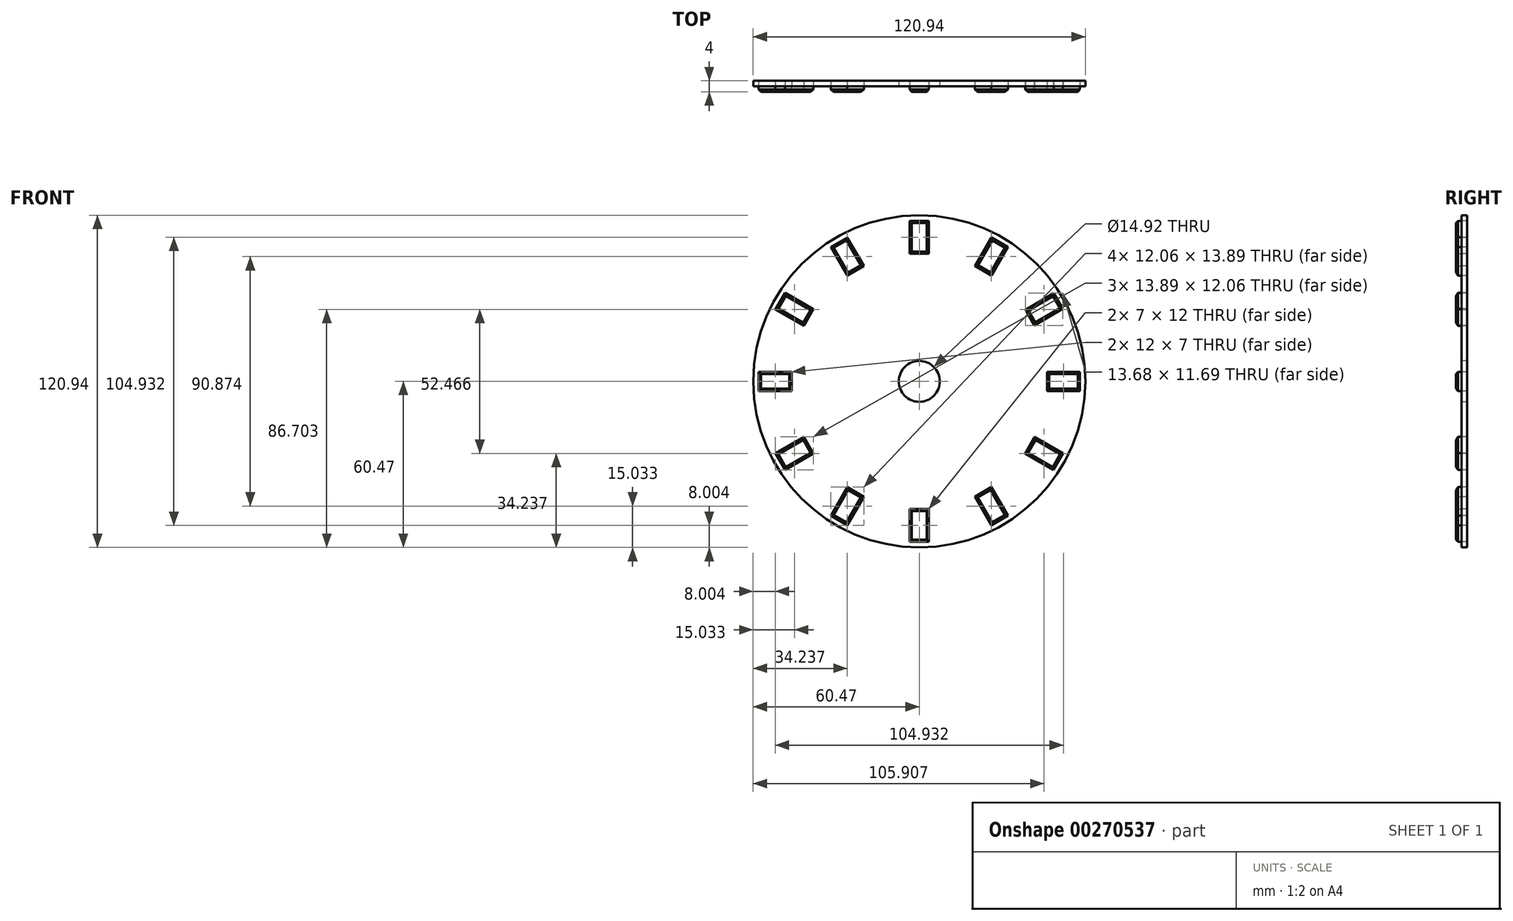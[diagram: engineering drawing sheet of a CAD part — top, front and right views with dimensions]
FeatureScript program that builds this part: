
annotation { "Feature Type Name" : "Feature", "Feature Type Description" : "" }
export const myFeature = defineFeature(function(context is Context, id is Id, definition is map)
    precondition{}
    {
        {
            var Q0;
            Q0=qCreatedBy(makeId("Front.planeOp"),FACE);
            var sketch = newSketch(context, id + "F0", { "sketchPlane" : qUnion([Q0])});
            skCircle(sketch, "E0", {"center": v(0, 0) * mm, "radius": 60.47 * mm});
            skLineSegment(sketch, "E1", {"start": v(0, 0) * mm, "end": v(23.27, 40.3) * mm});
            skLineSegment(sketch, "E2", {"start": v(0, 0) * mm, "end": v(-40.24, 23.23) * mm});
            skLineSegment(sketch, "E3", {"start": v(0, 0) * mm, "end": v(-40.24, -23.23) * mm});
            skLineSegment(sketch, "E4", {"start": v(-60.47, 0) * mm, "end": v(-58.47, 0) * mm});
            skLineSegment(sketch, "E5", {"start": v(0, 0) * mm, "end": v(40.24, -23.23) * mm});
            skLineSegment(sketch, "E6", {"start": v(0, 0) * mm, "end": v(0, 46.47) * mm});
            skLineSegment(sketch, "E7", {"start": v(0, 0) * mm, "end": v(46.47, 0) * mm});
            skLineSegment(sketch, "E8", {"start": v(0, 0) * mm, "end": v(0, -46.47) * mm});
            skLineSegment(sketch, "E9", {"start": v(0, 0) * mm, "end": v(40.24, 23.23) * mm});
            skLineSegment(sketch, "E10", {"start": v(0, 0) * mm, "end": v(23.23, -40.24) * mm});
            skLineSegment(sketch, "E11", {"start": v(0, 0) * mm, "end": v(-23.23, -40.24) * mm});
            skLineSegment(sketch, "E12", {"start": v(0, 0) * mm, "end": v(-23.23, 40.24) * mm});
            skLineSegment(sketch, "E13", {"start": v(52.28, 26.39) * mm, "end": v(41.88, 20.39) * mm});
            skLineSegment(sketch, "E14.MirrorCS", {"start": v(48.99, 32.08) * mm, "end": v(38.6, 26.08) * mm});
            skLineSegment(sketch, "E15", {"start": v(48.99, 32.08) * mm, "end": v(52.28, 26.39) * mm});
            skLineSegment(sketch, "E16", {"start": v(38.6, 26.08) * mm, "end": v(41.88, 20.39) * mm});
            skLineSegment(sketch, "E17", {"start": v(26.3, 38.55) * mm, "end": v(32.3, 48.94) * mm});
            skLineSegment(sketch, "E18.MirrorCS", {"start": v(20.24, 42.05) * mm, "end": v(26.24, 52.44) * mm});
            skLineSegment(sketch, "E19", {"start": v(20.24, 42.05) * mm, "end": v(26.3, 38.55) * mm});
            skLineSegment(sketch, "E20", {"start": v(26.24, 52.44) * mm, "end": v(32.3, 48.94) * mm});
            skLineSegment(sketch, "E21", {"start": v(3.5, 58.47) * mm, "end": v(3.5, 46.47) * mm});
            skLineSegment(sketch, "E22.MirrorCS", {"start": v(-3.5, 58.47) * mm, "end": v(-3.5, 46.47) * mm});
            skLineSegment(sketch, "E23", {"start": v(-3.5, 46.47) * mm, "end": v(3.5, 46.47) * mm});
            skLineSegment(sketch, "E24", {"start": v(3.5, 58.47) * mm, "end": v(-3.5, 58.47) * mm});
            skLineSegment(sketch, "E25", {"start": v(-52.38, 26.2) * mm, "end": v(-42, 20.2) * mm});
            skLineSegment(sketch, "E26", {"start": v(-52.38, -26.2) * mm, "end": v(-42, -20.2) * mm});
            skLineSegment(sketch, "E27", {"start": v(-26.2, -52.38) * mm, "end": v(-20.2, -42) * mm});
            skLineSegment(sketch, "E28", {"start": v(-3.5, -46.47) * mm, "end": v(-3.5, -58.47) * mm});
            skLineSegment(sketch, "E29", {"start": v(20.2, -42) * mm, "end": v(26.2, -52.38) * mm});
            skLineSegment(sketch, "E30", {"start": v(38.5, -26.26) * mm, "end": v(48.88, -32.26) * mm});
            skLineSegment(sketch, "E31", {"start": v(46.47, -3.5) * mm, "end": v(58.47, -3.5) * mm});
            skLineSegment(sketch, "E32", {"start": v(-26.2, 52.38) * mm, "end": v(-20.2, 42) * mm});
            skLineSegment(sketch, "E33.MirrorCS", {"start": v(-32.26, 48.88) * mm, "end": v(-26.26, 38.5) * mm});
            skLineSegment(sketch, "E34.MirrorCS", {"start": v(-48.88, 32.26) * mm, "end": v(-38.5, 26.26) * mm});
            skLineSegment(sketch, "E35.MirrorCS", {"start": v(-30.23, 52.37) * mm, "end": v(-29.23, 50.63) * mm});
            skLineSegment(sketch, "E36.MirrorCS", {"start": v(-48.88, -32.26) * mm, "end": v(-38.5, -26.26) * mm});
            skLineSegment(sketch, "E37.MirrorCS", {"start": v(0, 0) * mm, "end": v(-60.47, 0) * mm});
            skLineSegment(sketch, "E38.MirrorCS", {"start": v(0, 0) * mm, "end": v(-46.47, 0) * mm});
            skLineSegment(sketch, "E39.MirrorCS", {"start": v(-32.26, -48.88) * mm, "end": v(-26.26, -38.5) * mm});
            skLineSegment(sketch, "E40.MirrorCS", {"start": v(3.5, -46.47) * mm, "end": v(3.5, -58.47) * mm});
            skLineSegment(sketch, "E41.MirrorCS", {"start": v(26.26, -38.5) * mm, "end": v(32.26, -48.88) * mm});
            skLineSegment(sketch, "E42.MirrorCS", {"start": v(42, -20.2) * mm, "end": v(52.38, -26.2) * mm});
            skLineSegment(sketch, "E43.MirrorCS", {"start": v(46.47, 3.5) * mm, "end": v(58.47, 3.5) * mm});
            skLineSegment(sketch, "E44.MirrorCS", {"start": v(-41.55, 3.5) * mm, "end": v(-41.52, 3.5) * mm});
            skLineSegment(sketch, "E45", {"start": v(-38.5, 26.26) * mm, "end": v(-42, 20.2) * mm});
            skLineSegment(sketch, "E46", {"start": v(-48.88, 32.26) * mm, "end": v(-52.38, 26.2) * mm});
            skLineSegment(sketch, "E47", {"start": v(-42, -20.2) * mm, "end": v(-38.5, -26.26) * mm});
            skLineSegment(sketch, "E48", {"start": v(-52.38, -26.2) * mm, "end": v(-48.88, -32.26) * mm});
            skLineSegment(sketch, "E49", {"start": v(-26.26, -38.5) * mm, "end": v(-20.2, -42) * mm});
            skLineSegment(sketch, "E50", {"start": v(-26.2, -52.38) * mm, "end": v(-32.26, -48.88) * mm});
            skLineSegment(sketch, "E51", {"start": v(-3.5, -58.47) * mm, "end": v(3.5, -58.47) * mm});
            skLineSegment(sketch, "E52", {"start": v(3.5, -46.47) * mm, "end": v(-3.5, -46.47) * mm});
            skLineSegment(sketch, "E53", {"start": v(20.2, -42) * mm, "end": v(26.26, -38.5) * mm});
            skLineSegment(sketch, "E54", {"start": v(32.26, -48.88) * mm, "end": v(26.2, -52.38) * mm});
            skLineSegment(sketch, "E55", {"start": v(38.5, -26.26) * mm, "end": v(42, -20.2) * mm});
            skLineSegment(sketch, "E56", {"start": v(52.38, -26.2) * mm, "end": v(48.88, -32.26) * mm});
            skLineSegment(sketch, "E57", {"start": v(58.47, -3.5) * mm, "end": v(58.47, 3.5) * mm});
            skLineSegment(sketch, "E58", {"start": v(46.47, 3.5) * mm, "end": v(46.47, -3.5) * mm});
            skLineSegment(sketch, "E59", {"start": v(-32.26, 48.88) * mm, "end": v(-26.2, 52.38) * mm});
            skLineSegment(sketch, "E60", {"start": v(-20.2, 42) * mm, "end": v(-26.26, 38.5) * mm});
            skLineSegment(sketch, "E61", {"start": v(-58.47, 3.5) * mm, "end": v(-46.47, 3.5) * mm});
            skLineSegment(sketch, "E62.MirrorCS", {"start": v(-58.47, -3.5) * mm, "end": v(-46.47, -3.5) * mm});
            skLineSegment(sketch, "E63", {"start": v(-58.47, 3.5) * mm, "end": v(-58.47, -3.5) * mm});
            skLineSegment(sketch, "E64", {"start": v(-46.47, 3.5) * mm, "end": v(-46.47, -3.5) * mm});
            skLineSegment(sketch, "E65.trimOffspring", {"start": v(-50.63, 29.23) * mm, "end": v(-52.37, 30.23) * mm});
            skLineSegment(sketch, "E66.trimOffspring", {"start": v(-29.23, 50.63) * mm, "end": v(-30.23, 52.37) * mm});
            skLineSegment(sketch, "E67.trimOffspring", {"start": v(0, 58.47) * mm, "end": v(0, 60.47) * mm});
            skLineSegment(sketch, "E68.trimOffspring", {"start": v(29.27, 50.7) * mm, "end": v(30.27, 52.42) * mm});
            skLineSegment(sketch, "E69.trimOffspring", {"start": v(50.63, 29.23) * mm, "end": v(52.37, 30.23) * mm});
            skLineSegment(sketch, "E70.trimOffspring", {"start": v(58.47, 0) * mm, "end": v(60.47, 0) * mm});
            skLineSegment(sketch, "E71.trimOffspring", {"start": v(50.63, -29.23) * mm, "end": v(52.37, -30.23) * mm});
            skLineSegment(sketch, "E72.trimOffspring", {"start": v(29.23, -50.63) * mm, "end": v(30.23, -52.37) * mm});
            skLineSegment(sketch, "E73.trimOffspring", {"start": v(0, -58.47) * mm, "end": v(0, -60.47) * mm});
            skLineSegment(sketch, "E74.trimOffspring", {"start": v(-29.23, -50.63) * mm, "end": v(-30.23, -52.37) * mm});
            skLineSegment(sketch, "E75.trimOffspring", {"start": v(-50.63, -29.23) * mm, "end": v(-52.37, -30.23) * mm});
            skLineSegment(sketch, "E76.trimOffspring", {"start": v(-46.47, 0) * mm, "end": v(0, 0) * mm});
            skLineSegment(sketch, "E77.trimOffspring", {"start": v(-23.23, 40.24) * mm, "end": v(0, 0) * mm});
            skLineSegment(sketch, "E78.trimOffspring", {"start": v(-58.47, 0) * mm, "end": v(-60.47, 0) * mm});
            skSolve(sketch);
        }
        {
            var Q0;
            {var subQ2=sQuery(id+"F0.wireOp",EDGE,"E25");Q0=makeQuery(id+"F0.imprint","IMPRINT",FACE,{"disambiguationData":[TD([[makeQuery(id+"F0.imprint","IMPRINT",EDGE,{"derivedFrom":subQ2}),1.0]])]});}
            var Q1;
            {var subQ1=sQuery(id+"F0.wireOp",EDGE,"E32");Q1=makeQuery(id+"F0.imprint","IMPRINT",FACE,{"disambiguationData":[TD([[makeQuery(id+"F0.imprint","IMPRINT",EDGE,{"derivedFrom":subQ1}),-1.0]])]});}
            var Q2;
            {var subQ2=sQuery(id+"F0.wireOp",EDGE,"E21");Q2=makeQuery(id+"F0.imprint","IMPRINT",FACE,{"disambiguationData":[TD([[makeQuery(id+"F0.imprint","IMPRINT",EDGE,{"derivedFrom":subQ2}),-1.0]])]});}
            var Q3;
            {var subQ2=sQuery(id+"F0.wireOp",EDGE,"E17");Q3=makeQuery(id+"F0.imprint","IMPRINT",FACE,{"disambiguationData":[TD([[makeQuery(id+"F0.imprint","IMPRINT",EDGE,{"derivedFrom":subQ2}),1.0]])]});}
            var Q4;
            {var subQ1=sQuery(id+"F0.wireOp",EDGE,"E13");Q4=makeQuery(id+"F0.imprint","IMPRINT",FACE,{"disambiguationData":[TD([[makeQuery(id+"F0.imprint","IMPRINT",EDGE,{"derivedFrom":subQ1}),-1.0]])]});}
            var Q5;
            {var subQ5=sQuery(id+"F0.wireOp",EDGE,"E31");Q5=makeQuery(id+"F0.imprint","IMPRINT",FACE,{"disambiguationData":[TD([[makeQuery(id+"F0.imprint","IMPRINT",EDGE,{"derivedFrom":subQ5}),1.0]])]});}
            var Q6;
            {var subQ3=sQuery(id+"F0.wireOp",EDGE,"E30");Q6=makeQuery(id+"F0.imprint","IMPRINT",FACE,{"disambiguationData":[TD([[makeQuery(id+"F0.imprint","IMPRINT",EDGE,{"derivedFrom":subQ3}),1.0]])]});}
            var Q7;
            {var subQ3=sQuery(id+"F0.wireOp",EDGE,"E29");Q7=makeQuery(id+"F0.imprint","IMPRINT",FACE,{"disambiguationData":[TD([[makeQuery(id+"F0.imprint","IMPRINT",EDGE,{"derivedFrom":subQ3}),1.0]])]});}
            var Q8;
            {var subQ3=sQuery(id+"F0.wireOp",EDGE,"E28");Q8=makeQuery(id+"F0.imprint","IMPRINT",FACE,{"disambiguationData":[TD([[makeQuery(id+"F0.imprint","IMPRINT",EDGE,{"derivedFrom":subQ3}),1.0]])]});}
            var Q9;
            {var subQ2=sQuery(id+"F0.wireOp",EDGE,"E27");Q9=makeQuery(id+"F0.imprint","IMPRINT",FACE,{"disambiguationData":[TD([[makeQuery(id+"F0.imprint","IMPRINT",EDGE,{"derivedFrom":subQ2}),1.0]])]});}
            var Q10;
            {var subQ3=sQuery(id+"F0.wireOp",EDGE,"E26");Q10=makeQuery(id+"F0.imprint","IMPRINT",FACE,{"disambiguationData":[TD([[makeQuery(id+"F0.imprint","IMPRINT",EDGE,{"derivedFrom":subQ3}),-1.0]])]});}
            var Q11;
            {var subQ0=sQuery(id+"F0.wireOp",EDGE,"E37.MirrorCS");Q11=makeQuery(id+"F0.imprint","IMPRINT",FACE,{"disambiguationData":[TD([[makeQuery(id+"F0.imprint","IMPRINT",EDGE,{"derivedFrom":subQ0}),-1.0]])]});}
            var Q12;
            {var subQ0=sQuery(id+"F0.wireOp",EDGE,"E37.MirrorCS");Q12=makeQuery(id+"F0.imprint","IMPRINT",FACE,{"disambiguationData":[TD([[makeQuery(id+"F0.imprint","IMPRINT",EDGE,{"derivedFrom":subQ0}),1.0]])]});}
            extrude(context, id + "F1", {"entities" : qUnion([Q0, Q1, Q2, Q3, Q4, Q5, Q6, Q7, Q8, Q9, Q10, Q11, Q12]), "depth" : 2 * mm});
        }
        {
            var Q0;
            Q0 = qSketchRegion(id + "F0", true);
            extrude(context, id + "F2", {"entities" : qUnion([Q0]), "oppositeDirection" : true, "depth" : 2 * mm});
        }
        {
            var Q0;
            Q0=qCreatedBy(makeId("Front.planeOp"),FACE);
            var sketch = newSketch(context, id + "F3", { "sketchPlane" : qUnion([Q0])});
            skCircle(sketch, "E79", {"center": v(0, 0) * mm, "radius": 7.46 * mm});
            skCircle(sketch, "E80", {"center": v(46.57, 14.57) * mm, "radius": 2.5 * mm});
            skCircle(sketch, "E81", {"center": v(-47.92, -12.77) * mm, "radius": 2.5 * mm});
            skSolve(sketch);
        }
        {
            var Q0;
            Q0=makeQuery(id+"F3.imprint","IMPRINT",FACE,{"disambiguationData":[TD([[makeQuery(id+"F3.imprint","IMPRINT",EDGE,{"derivedFrom":sQuery(id+"F3.wireOp",EDGE,"E79")}),1.0]])]});
            extrude(context, id + "F4", {"entities" : qUnion([Q0]), "operationType" : NewBodyOperationType.REMOVE, "oppositeDirection" : true, "depth" : 5 * mm});
        }
        {
            var Q0;
            Q0=sQuery(id+"F3.wireOp",EDGE,"E80");
            var Q1;
            Q1=sQuery(id+"F3.wireOp",EDGE,"E81");
            extrude(context, id + "F5", {"bodyType" : ToolBodyType.SURFACE, "surfaceEntities" : qUnion([Q0, Q1]), "oppositeDirection" : true, "depth" : 25 * mm});
        }
        {
            var Q0;
            Q0=makeQuery(id+"F1.opExtrude","CAP_FACE",FACE,{"disambiguationData":[OSD([sQuery(id+"F0.wireOp",EDGE,"E31"),sQuery(id+"F0.wireOp",EDGE,"E43.MirrorCS"),sQuery(id+"F0.wireOp",EDGE,"E57"),sQuery(id+"F0.wireOp",EDGE,"E58")])],"isStart":true});
            var Q1;
            Q1=makeQuery(id+"F1.opExtrude","CAP_FACE",FACE,{"disambiguationData":[OSD([sQuery(id+"F0.wireOp",EDGE,"E13"),sQuery(id+"F0.wireOp",EDGE,"E14.MirrorCS"),sQuery(id+"F0.wireOp",EDGE,"E15"),sQuery(id+"F0.wireOp",EDGE,"E16")])],"isStart":true});
            var Q2;
            Q2=makeQuery(id+"F1.opExtrude","CAP_FACE",FACE,{"disambiguationData":[OSD([sQuery(id+"F0.wireOp",EDGE,"E17"),sQuery(id+"F0.wireOp",EDGE,"E18.MirrorCS"),sQuery(id+"F0.wireOp",EDGE,"E19"),sQuery(id+"F0.wireOp",EDGE,"E20")])],"isStart":true});
            var Q3;
            Q3=makeQuery(id+"F1.opExtrude","CAP_FACE",FACE,{"disambiguationData":[OSD([sQuery(id+"F0.wireOp",EDGE,"E21"),sQuery(id+"F0.wireOp",EDGE,"E22.MirrorCS"),sQuery(id+"F0.wireOp",EDGE,"E23"),sQuery(id+"F0.wireOp",EDGE,"E24")])],"isStart":true});
            var Q4;
            Q4=makeQuery(id+"F1.opExtrude","CAP_FACE",FACE,{"disambiguationData":[OSD([sQuery(id+"F0.wireOp",EDGE,"E32"),sQuery(id+"F0.wireOp",EDGE,"E33.MirrorCS"),sQuery(id+"F0.wireOp",EDGE,"E59"),sQuery(id+"F0.wireOp",EDGE,"E60")])],"isStart":true});
            var Q5;
            Q5=makeQuery(id+"F1.opExtrude","CAP_FACE",FACE,{"disambiguationData":[OSD([sQuery(id+"F0.wireOp",EDGE,"E25"),sQuery(id+"F0.wireOp",EDGE,"E34.MirrorCS"),sQuery(id+"F0.wireOp",EDGE,"E45"),sQuery(id+"F0.wireOp",EDGE,"E46")])],"isStart":true});
            var Q6;
            Q6=makeQuery(id+"F1.opExtrude","CAP_FACE",FACE,{"disambiguationData":[OSD([sQuery(id+"F0.wireOp",EDGE,"E61"),sQuery(id+"F0.wireOp",EDGE,"E62.MirrorCS"),sQuery(id+"F0.wireOp",EDGE,"E63"),sQuery(id+"F0.wireOp",EDGE,"E64")])],"isStart":true});
            var Q7;
            Q7=makeQuery(id+"F1.opExtrude","CAP_FACE",FACE,{"disambiguationData":[OSD([sQuery(id+"F0.wireOp",EDGE,"E26"),sQuery(id+"F0.wireOp",EDGE,"E36.MirrorCS"),sQuery(id+"F0.wireOp",EDGE,"E47"),sQuery(id+"F0.wireOp",EDGE,"E48")])],"isStart":true});
            var Q8;
            Q8=makeQuery(id+"F1.opExtrude","CAP_FACE",FACE,{"disambiguationData":[OSD([sQuery(id+"F0.wireOp",EDGE,"E27"),sQuery(id+"F0.wireOp",EDGE,"E39.MirrorCS"),sQuery(id+"F0.wireOp",EDGE,"E49"),sQuery(id+"F0.wireOp",EDGE,"E50")])],"isStart":true});
            var Q9;
            Q9=makeQuery(id+"F1.opExtrude","CAP_FACE",FACE,{"disambiguationData":[OSD([sQuery(id+"F0.wireOp",EDGE,"E28"),sQuery(id+"F0.wireOp",EDGE,"E40.MirrorCS"),sQuery(id+"F0.wireOp",EDGE,"E51"),sQuery(id+"F0.wireOp",EDGE,"E52")])],"isStart":true});
            var Q10;
            Q10=makeQuery(id+"F1.opExtrude","CAP_FACE",FACE,{"disambiguationData":[OSD([sQuery(id+"F0.wireOp",EDGE,"E29"),sQuery(id+"F0.wireOp",EDGE,"E41.MirrorCS"),sQuery(id+"F0.wireOp",EDGE,"E53"),sQuery(id+"F0.wireOp",EDGE,"E54")])],"isStart":true});
            var Q11;
            Q11=makeQuery(id+"F1.opExtrude","CAP_FACE",FACE,{"disambiguationData":[OSD([sQuery(id+"F0.wireOp",EDGE,"E30"),sQuery(id+"F0.wireOp",EDGE,"E42.MirrorCS"),sQuery(id+"F0.wireOp",EDGE,"E55"),sQuery(id+"F0.wireOp",EDGE,"E56")])],"isStart":true});
            extrude(context, id + "F6", {"entities" : qUnion([Q0, Q1, Q2, Q3, Q4, Q5, Q6, Q7, Q8, Q9, Q10, Q11]), "depth" : 2 * mm});
        }
        {
            var Q0;
            Q0=makeQuery(id+"F1.opExtrude","CAP_EDGE",EDGE,{"disambiguationData":[OSD([sQuery(id+"F0.wireOp",EDGE,"E25")])],"isStart":false});
            var Q1;
            Q1=makeQuery(id+"F1.opExtrude","CAP_EDGE",EDGE,{"disambiguationData":[OSD([sQuery(id+"F0.wireOp",EDGE,"E34.MirrorCS")])],"isStart":false});
            var Q2;
            Q2=makeQuery(id+"F1.opExtrude","CAP_EDGE",EDGE,{"disambiguationData":[OSD([sQuery(id+"F0.wireOp",EDGE,"E33.MirrorCS")])],"isStart":false});
            var Q3;
            Q3=makeQuery(id+"F1.opExtrude","CAP_EDGE",EDGE,{"disambiguationData":[OSD([sQuery(id+"F0.wireOp",EDGE,"E32")])],"isStart":false});
            var Q4;
            Q4=makeQuery(id+"F1.opExtrude","CAP_EDGE",EDGE,{"disambiguationData":[OSD([sQuery(id+"F0.wireOp",EDGE,"E22.MirrorCS")])],"isStart":false});
            var Q5;
            Q5=makeQuery(id+"F1.opExtrude","CAP_EDGE",EDGE,{"disambiguationData":[OSD([sQuery(id+"F0.wireOp",EDGE,"E21")])],"isStart":false});
            var Q6;
            Q6=makeQuery(id+"F1.opExtrude","CAP_EDGE",EDGE,{"disambiguationData":[OSD([sQuery(id+"F0.wireOp",EDGE,"E18.MirrorCS")])],"isStart":false});
            var Q7;
            Q7=makeQuery(id+"F1.opExtrude","CAP_EDGE",EDGE,{"disambiguationData":[OSD([sQuery(id+"F0.wireOp",EDGE,"E17")])],"isStart":false});
            var Q8;
            Q8=makeQuery(id+"F1.opExtrude","CAP_EDGE",EDGE,{"disambiguationData":[OSD([sQuery(id+"F0.wireOp",EDGE,"E13")])],"isStart":false});
            var Q9;
            Q9=makeQuery(id+"F1.opExtrude","CAP_EDGE",EDGE,{"disambiguationData":[OSD([sQuery(id+"F0.wireOp",EDGE,"E14.MirrorCS")])],"isStart":false});
            var Q10;
            Q10=makeQuery(id+"F1.opExtrude","CAP_EDGE",EDGE,{"disambiguationData":[OSD([sQuery(id+"F0.wireOp",EDGE,"E31")])],"isStart":false});
            var Q11;
            Q11=makeQuery(id+"F1.opExtrude","CAP_EDGE",EDGE,{"disambiguationData":[OSD([sQuery(id+"F0.wireOp",EDGE,"E30")])],"isStart":false});
            var Q12;
            Q12=makeQuery(id+"F1.opExtrude","CAP_EDGE",EDGE,{"disambiguationData":[OSD([sQuery(id+"F0.wireOp",EDGE,"E29")])],"isStart":false});
            var Q13;
            Q13=makeQuery(id+"F1.opExtrude","CAP_EDGE",EDGE,{"disambiguationData":[OSD([sQuery(id+"F0.wireOp",EDGE,"E40.MirrorCS")])],"isStart":false});
            var Q14;
            Q14=makeQuery(id+"F1.opExtrude","CAP_EDGE",EDGE,{"disambiguationData":[OSD([sQuery(id+"F0.wireOp",EDGE,"E51")])],"isStart":false});
            var Q15;
            Q15=makeQuery(id+"F1.opExtrude","CAP_EDGE",EDGE,{"disambiguationData":[OSD([sQuery(id+"F0.wireOp",EDGE,"E28")])],"isStart":false});
            var Q16;
            Q16=makeQuery(id+"F1.opExtrude","CAP_EDGE",EDGE,{"disambiguationData":[OSD([sQuery(id+"F0.wireOp",EDGE,"E52")])],"isStart":false});
            var Q17;
            Q17=makeQuery(id+"F1.opExtrude","CAP_EDGE",EDGE,{"disambiguationData":[OSD([sQuery(id+"F0.wireOp",EDGE,"E49")])],"isStart":false});
            var Q18;
            Q18=makeQuery(id+"F1.opExtrude","CAP_EDGE",EDGE,{"disambiguationData":[OSD([sQuery(id+"F0.wireOp",EDGE,"E27")])],"isStart":false});
            var Q19;
            Q19=makeQuery(id+"F1.opExtrude","CAP_EDGE",EDGE,{"disambiguationData":[OSD([sQuery(id+"F0.wireOp",EDGE,"E50")])],"isStart":false});
            var Q20;
            Q20=makeQuery(id+"F1.opExtrude","CAP_EDGE",EDGE,{"disambiguationData":[OSD([sQuery(id+"F0.wireOp",EDGE,"E39.MirrorCS")])],"isStart":false});
            var Q21;
            Q21=makeQuery(id+"F1.opExtrude","CAP_EDGE",EDGE,{"disambiguationData":[OSD([sQuery(id+"F0.wireOp",EDGE,"E36.MirrorCS")])],"isStart":false});
            var Q22;
            Q22=makeQuery(id+"F1.opExtrude","CAP_EDGE",EDGE,{"disambiguationData":[OSD([sQuery(id+"F0.wireOp",EDGE,"E48")])],"isStart":false});
            var Q23;
            Q23=makeQuery(id+"F1.opExtrude","CAP_EDGE",EDGE,{"disambiguationData":[OSD([sQuery(id+"F0.wireOp",EDGE,"E26")])],"isStart":false});
            var Q24;
            Q24=makeQuery(id+"F1.opExtrude","CAP_EDGE",EDGE,{"disambiguationData":[OSD([sQuery(id+"F0.wireOp",EDGE,"E47")])],"isStart":false});
            var Q25;
            Q25=makeQuery(id+"F1.opExtrude","CAP_FACE",FACE,{"disambiguationData":[OSD([sQuery(id+"F0.wireOp",EDGE,"E61"),sQuery(id+"F0.wireOp",EDGE,"E62.MirrorCS"),sQuery(id+"F0.wireOp",EDGE,"E63"),sQuery(id+"F0.wireOp",EDGE,"E64")])],"isStart":false});
            var Q26;
            Q26=makeQuery(id+"F1.opExtrude","CAP_FACE",FACE,{"disambiguationData":[OSD([sQuery(id+"F0.wireOp",EDGE,"E25"),sQuery(id+"F0.wireOp",EDGE,"E34.MirrorCS"),sQuery(id+"F0.wireOp",EDGE,"E45"),sQuery(id+"F0.wireOp",EDGE,"E46")])],"isStart":false});
            var Q27;
            Q27=makeQuery(id+"F1.opExtrude","CAP_FACE",FACE,{"disambiguationData":[OSD([sQuery(id+"F0.wireOp",EDGE,"E32"),sQuery(id+"F0.wireOp",EDGE,"E33.MirrorCS"),sQuery(id+"F0.wireOp",EDGE,"E59"),sQuery(id+"F0.wireOp",EDGE,"E60")])],"isStart":false});
            var Q28;
            Q28=makeQuery(id+"F1.opExtrude","CAP_FACE",FACE,{"disambiguationData":[OSD([sQuery(id+"F0.wireOp",EDGE,"E21"),sQuery(id+"F0.wireOp",EDGE,"E22.MirrorCS"),sQuery(id+"F0.wireOp",EDGE,"E23"),sQuery(id+"F0.wireOp",EDGE,"E24")])],"isStart":false});
            var Q29;
            Q29=makeQuery(id+"F1.opExtrude","CAP_FACE",FACE,{"disambiguationData":[OSD([sQuery(id+"F0.wireOp",EDGE,"E17"),sQuery(id+"F0.wireOp",EDGE,"E18.MirrorCS"),sQuery(id+"F0.wireOp",EDGE,"E19"),sQuery(id+"F0.wireOp",EDGE,"E20")])],"isStart":false});
            var Q30;
            Q30=makeQuery(id+"F1.opExtrude","CAP_FACE",FACE,{"disambiguationData":[OSD([sQuery(id+"F0.wireOp",EDGE,"E13"),sQuery(id+"F0.wireOp",EDGE,"E14.MirrorCS"),sQuery(id+"F0.wireOp",EDGE,"E15"),sQuery(id+"F0.wireOp",EDGE,"E16")])],"isStart":false});
            var Q31;
            Q31=makeQuery(id+"F1.opExtrude","CAP_FACE",FACE,{"disambiguationData":[OSD([sQuery(id+"F0.wireOp",EDGE,"E31"),sQuery(id+"F0.wireOp",EDGE,"E43.MirrorCS"),sQuery(id+"F0.wireOp",EDGE,"E57"),sQuery(id+"F0.wireOp",EDGE,"E58")])],"isStart":false});
            var Q32;
            Q32=makeQuery(id+"F1.opExtrude","CAP_FACE",FACE,{"disambiguationData":[OSD([sQuery(id+"F0.wireOp",EDGE,"E30"),sQuery(id+"F0.wireOp",EDGE,"E42.MirrorCS"),sQuery(id+"F0.wireOp",EDGE,"E55"),sQuery(id+"F0.wireOp",EDGE,"E56")])],"isStart":false});
            var Q33;
            Q33=makeQuery(id+"F1.opExtrude","CAP_FACE",FACE,{"disambiguationData":[OSD([sQuery(id+"F0.wireOp",EDGE,"E29"),sQuery(id+"F0.wireOp",EDGE,"E41.MirrorCS"),sQuery(id+"F0.wireOp",EDGE,"E53"),sQuery(id+"F0.wireOp",EDGE,"E54")])],"isStart":false});
            chamfer(context, id + "F7", {"entities" : qUnion([Q0, Q1, Q2, Q3, Q4, Q5, Q6, Q7, Q8, Q9, Q10, Q11, Q12, Q13, Q14, Q15, Q16, Q17, Q18, Q19, Q20, Q21, Q22, Q23, Q24, Q25, Q26, Q27, Q28, Q29, Q30, Q31, Q32, Q33]), "width" : 0.8 * mm, "tangentPropagation" : true});
        }
    });
